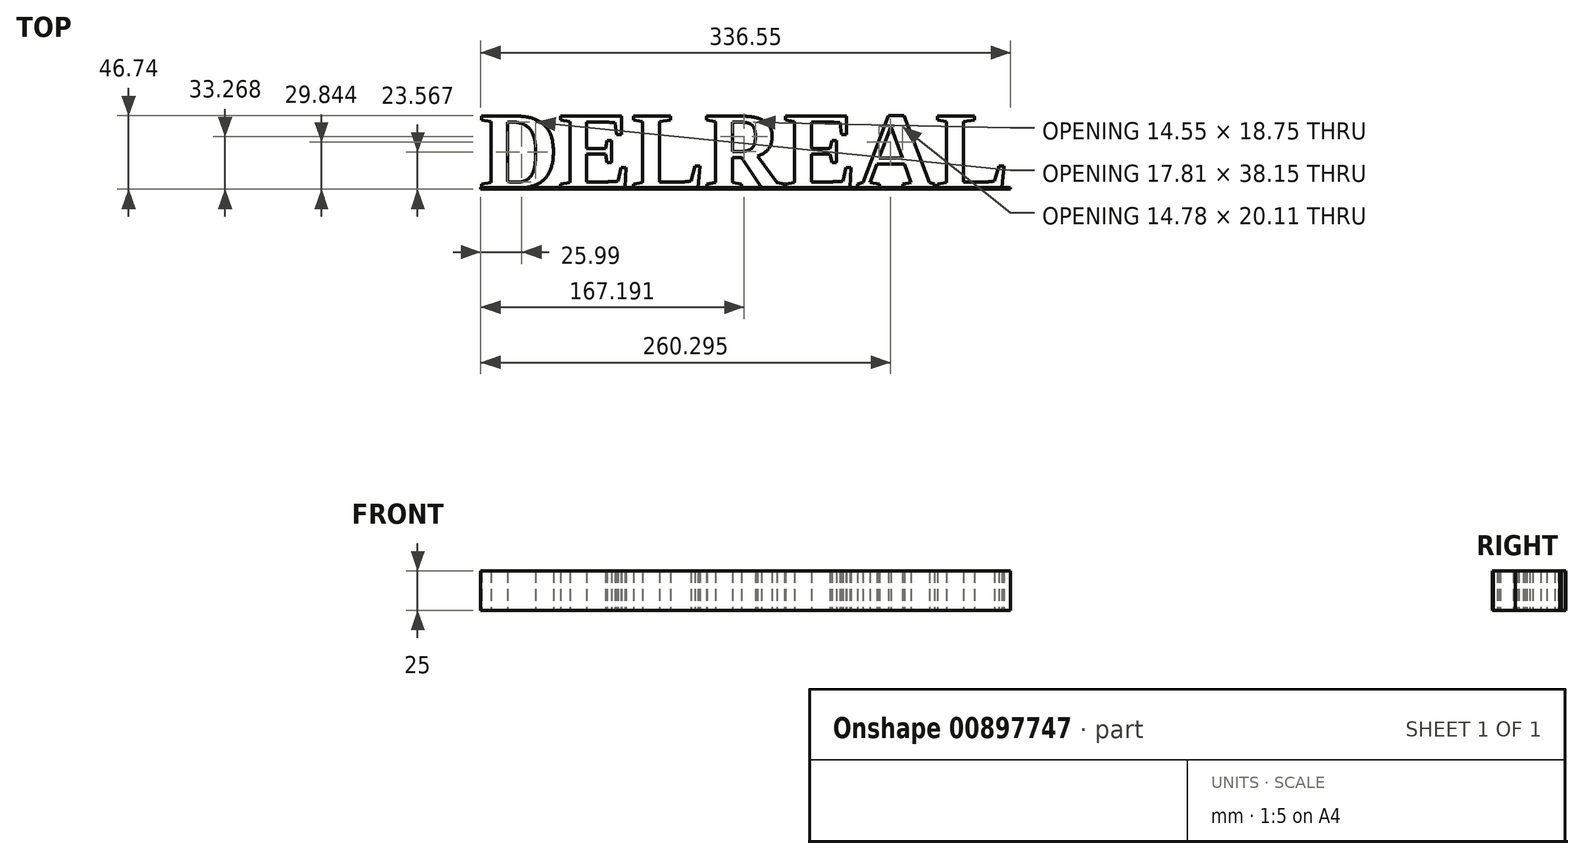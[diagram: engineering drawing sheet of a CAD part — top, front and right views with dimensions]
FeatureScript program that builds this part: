
annotation { "Feature Type Name" : "Feature", "Feature Type Description" : "" }
export const myFeature = defineFeature(function(context is Context, id is Id, definition is map)
    precondition{}
    {
        {
            var Q0;
            Q0=qCreatedBy(makeId("Top.planeOp"),FACE);
            var sketch = newSketch(context, id + "F0", { "sketchPlane" : qUnion([Q0])});
            skText(sketch, "E0", { "text": "DELREAL", "fontName": "Tinos-Bold.ttf"});
            const initialGuessF0  = {"E0": [-0.33716, 0, 1, 0, 0.05]};
            skSetInitialGuess(sketch, initialGuessF0);
            skSolve(sketch);
        }
        {
            var Q0;
            Q0=qCreatedBy(makeId("Top.planeOp"),FACE);
            var sketch = newSketch(context, id + "F1", { "sketchPlane" : qUnion([Q0])});
            skLineSegment(sketch, "E1.bottom", {"start": v(-336.55, 0) * mm, "end": v(0, 0) * mm});
            skLineSegment(sketch, "E1.top", {"start": v(-336.55, -0.9) * mm, "end": v(0, -0.9) * mm});
            skLineSegment(sketch, "E1.left", {"start": v(-336.55, 0) * mm, "end": v(-336.55, -0.9) * mm});
            skLineSegment(sketch, "E1.right", {"start": v(0, 0) * mm, "end": v(0, -0.9) * mm});
            skSolve(sketch);
        }
        {
            var Q0;
            Q0 = qSketchRegion(id + "F1", true);
            var Q1;
            Q1 = qSketchRegion(id + "F0", true);
            extrude(context, id + "F2", {"entities" : qUnion([Q0, Q1]), "depth" : 25 * mm, "offsetDistance" : 25 * mm});
        }
    });
